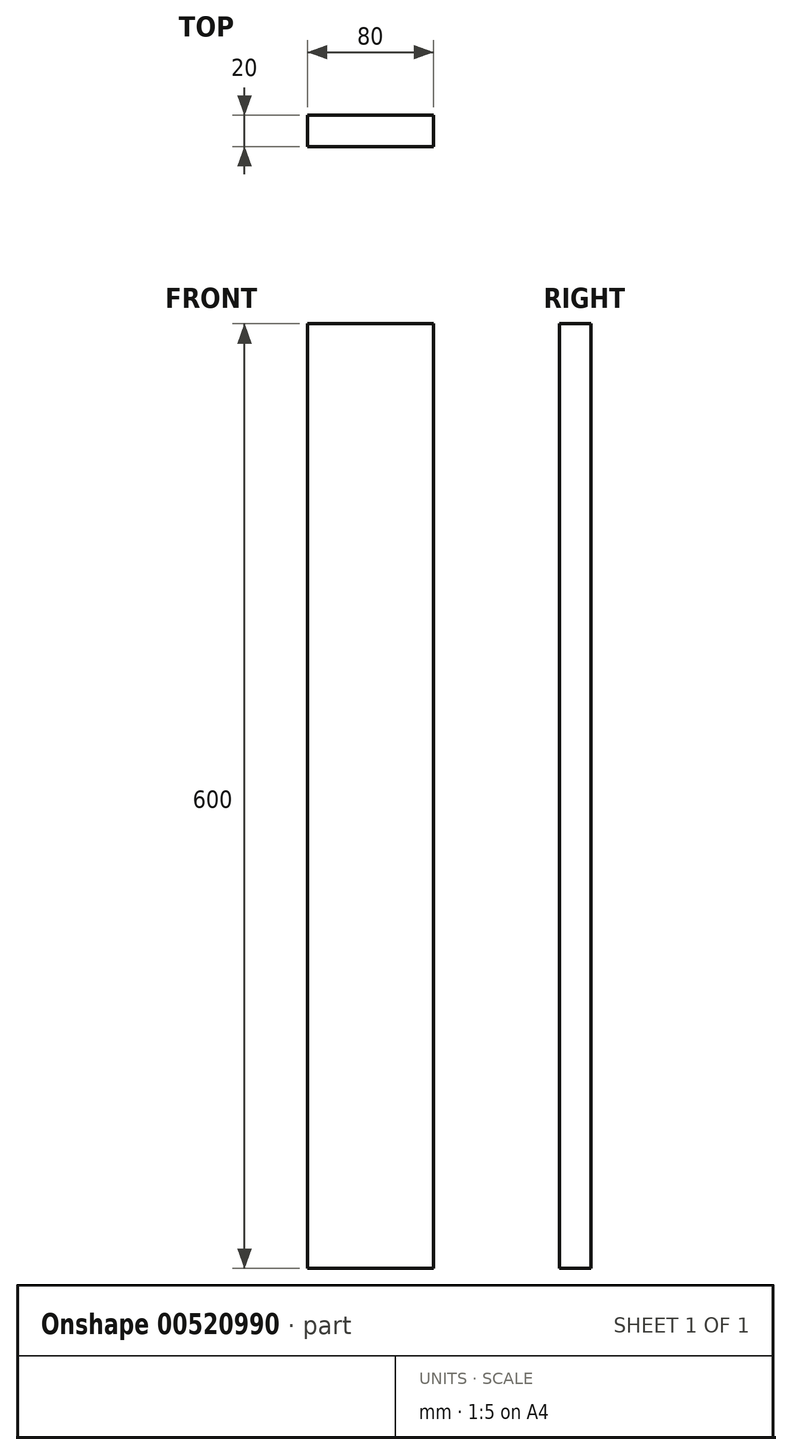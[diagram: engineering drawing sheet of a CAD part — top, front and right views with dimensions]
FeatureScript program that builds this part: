
annotation { "Feature Type Name" : "Feature", "Feature Type Description" : "" }
export const myFeature = defineFeature(function(context is Context, id is Id, definition is map)
    precondition{}
    {
        {
            var Q0;
            Q0=qCreatedBy(makeId("Top.planeOp"),FACE);
            var sketch = newSketch(context, id + "F0", { "sketchPlane" : qUnion([Q0])});
            skLineSegment(sketch, "E0.bottom", {"start": v(-40, 10) * mm, "end": v(40, 10) * mm});
            skLineSegment(sketch, "E0.top", {"start": v(-40, -10) * mm, "end": v(40, -10) * mm});
            skLineSegment(sketch, "E0.left", {"start": v(-40, 10) * mm, "end": v(-40, -10) * mm});
            skLineSegment(sketch, "E0.right", {"start": v(40, 10) * mm, "end": v(40, -10) * mm});
            skPoint(sketch, "E0.middle", {"position": v(0, 0) * mm});
            skSolve(sketch);
        }
        {
            var Q0;
            Q0=makeQuery(id+"F0.imprint","IMPRINT",FACE,{"disambiguationData":[TD([[makeQuery(id+"F0.imprint","IMPRINT",EDGE,{"derivedFrom":sQuery(id+"F0.wireOp",EDGE,"E0.bottom")}),-1.0]])]});
            extrude(context, id + "F1", {"entities" : qUnion([Q0]), "depth" : 600 * mm, "offsetDistance" : 25 * mm});
        }
    });
